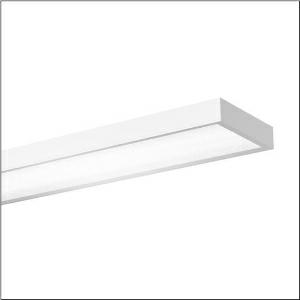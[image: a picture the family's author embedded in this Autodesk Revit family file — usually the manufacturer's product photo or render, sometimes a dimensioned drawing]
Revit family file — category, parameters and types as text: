
# Revit family: sport_31_51hs12dd4jca
name_source: partatom
category: Lighting Fixtures
units: mm (PartAtom-declared; Revit-internal decimal feet)

## family parameters
Cut with Voids When Loaded = No
Host = Face
Light Source = No
Part Type = Normal
Room Calculation Point = No
Round Connector Dimension = Use Diameter
Shared = No

## types (1)
- --- (1 x LED, 19720 lm, 146.2 W, 4000K)
    Apparent Load = 146 VA
    CIE Flux Codes = 65 89 97 100 100
    Color Rendering = 80
    Color Temperature = 4000K
    Default Elevation = 1800 mm
    Description = Sport 31, high bay luminaire, primary light control with reflector, of sheet steel, primary anti-glare with prismatic structure, of PC, primary optical cover: cover panel, of PC, light emission: direct distribution, primary light characteristic: symmetric, installation type: suspended mounting, recessed, surface-mounted, LED, rated luminous flux: 20.000lm, luminous efficacy: 137lm/W, light colour: 840, colour temperature: 4000K, control gear: DALI 2, with terminal, 5-pole, max. 2.5mm², mains connection: 220..240V, AC/DC, 50/60Hz, rated input power: 146W, housing, of sheet steel, traffic white (RAL 9016), length: 1.540mm, width: 415mm, height: 95mm, protection rating (complete): IP20, protection rating (lamp compartment, on room side): IP50, insulation class (complete): insulation class I (protective earthing), certification: CE, ENEC, UKCA, ball protection: ball impact resistant with ceiling mounting or chain suspension, impact resistance: IK08, permissible operating ambient temperature: -20..+35°C, standard: DIN 18032-3, EN 60598-2-22, packaging unit: 1 piece
    Height = 100 mm  [stored 0.328084 ft]
    Lamp = 1 x LED
    Lamp Light Flux = 19720 lm
    Lamp Power = 146.2 W
    Lamp count = 1
    Length = 1500 mm
    Luminous efficacy = 135 lm/W
    Manufacturer = Siteco
    ModVariant = No
    Model = 51HS12DD4JCA
    Mounting Place = Ceiling
    Mounting Type = Pendant
    Number of Poles = 1
    OnlyDefault = Yes
    Power Factor = 1
    Product Name = Sport 31
    Product group = high bay luminaire
    ProductGroupID = 901
    Protection Class = Protection class I
    Protection Degree = IP 20
    RLX_Detail_Level = 1
    RLX_Emergency_Light_Flux = 0 lm
    RLX_Emergency_Type = 0
    RLX_Emergency_Type_DB = No
    RlxData = <blob elided: 24097 chars, md5=584a94e8>
    Socket = socket
    Standby Power = 0 W
    System Light Flux = 19719 lm
    System Power = 146 W
    Type Comments = factory setting: luminous flux: 100 % | dim-lin: 254 | 610 mA
    Type Image = l_1006829.jpg
    URL = http://relux.com
    VarID = @adj_218399
    Voltage = 0 V
    Weight = 0.00 kg
    Width = 415 mm

note: [stored X ft] marks values corroborated as IEEE doubles in the binary element streams (Revit-internal decimal feet)

## geometry (parser evidence)
native form markers: Blend x4, Sweep x10
no freeform markers — native parametric forms only
